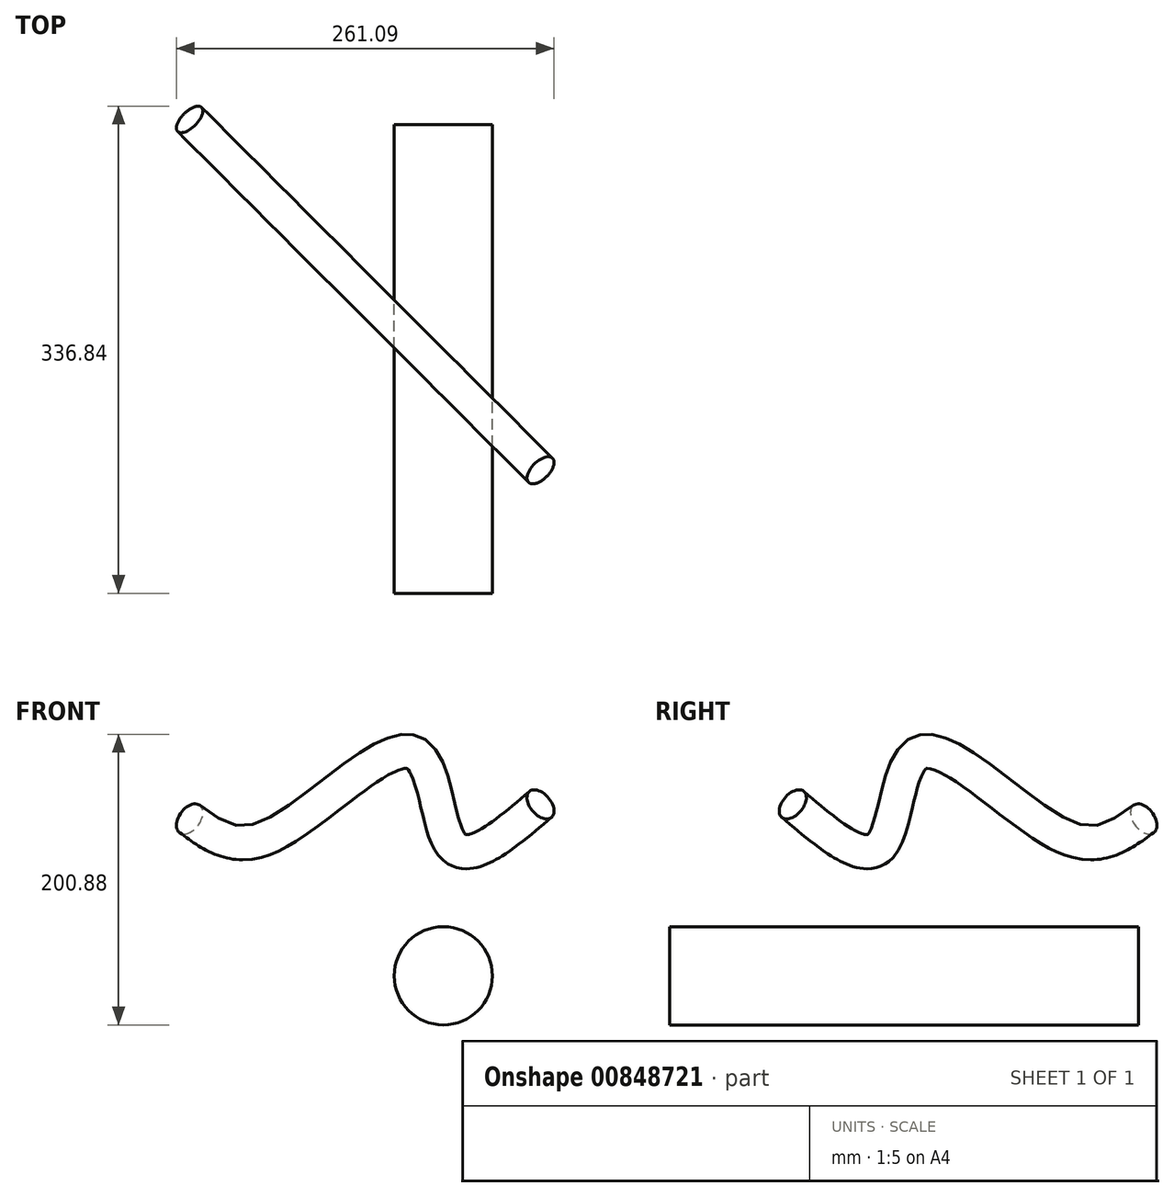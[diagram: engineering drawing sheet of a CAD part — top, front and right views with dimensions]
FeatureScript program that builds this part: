
annotation { "Feature Type Name" : "Feature", "Feature Type Description" : "" }
export const myFeature = defineFeature(function(context is Context, id is Id, definition is map)
    precondition{}
    {
        {
            var Q0;
            Q0=qCreatedBy(makeId("Front.planeOp"),FACE);
            var sketch = newSketch(context, id + "F0", { "sketchPlane" : qUnion([Q0])});
            skCircle(sketch, "E0", {"center": v(0, 0) * mm, "radius": 33.95 * mm});
            skSolve(sketch);
        }
        {
            var Q0;
            Q0 = qSketchRegion(id + "F0", true);
            extrude(context, id + "F1", {"entities" : qUnion([Q0]), "depth" : 324.1 * mm, "offsetDistance" : 25.4 * mm});
        }
        {
            var Q0;
            Q0=qCreatedBy(makeId("Right.planeOp"),FACE);
            var sketch = newSketch(context, id + "F2", { "sketchPlane" : qUnion([Q0])});
            skFitSpline(sketch, "E1", {"points": [v(76.36, 108.21) * mm, v(0, 95.44) * mm, v(-145.46, 152.9) * mm, v(-179.98, 90.26) * mm, v(-266.98, 118.27) * mm], "startDerivative": vector(-290.4, -151.51) * mm, "endDerivative": vector(-433.5, 262.42) * mm});
            skSolve(sketch);
        }
        {
            var Q0;
            Q0=sQuery(id+"F2.wireOp",EDGE,"E1");
            var Q1;
            Q1=sQuery(id+"F2.wireOp",VERTEX,"E1.2.internal");
            cPlane(context, id + "F3", {"entities" : qUnion([Q0, Q1]), "cplaneType" : CPlaneType.CURVE_POINT, "offset" : 25.4 * mm, "width" : 152.4 * mm, "height" : 152.4 * mm});
        }
        {
            var Q0;
            Q0=qCreatedBy(id+"F3.planeOp",FACE);
            var sketch = newSketch(context, id + "F4", { "sketchPlane" : qUnion([Q0])});
            skCircle(sketch, "E2", {"center": v(0, 200.08) * mm, "radius": 11.76 * mm});
            skSolve(sketch);
        }
        {
            var Q0;
            Q0=makeQuery(id+"F4.imprint","IMPRINT",FACE,{"disambiguationData":[TD([[makeQuery(id+"F4.imprint","IMPRINT",EDGE,{"derivedFrom":sQuery(id+"F4.wireOp",EDGE,"E2")}),1.0]])]});
            var Q1;
            Q1=sQuery(id+"F2.wireOp",EDGE,"E1");
            sweep(context, id + "F5", {"profiles" : qUnion([Q0]), "path" : qUnion([Q1])});
        }
        {
            var Q0;
            Q0=qCreatedBy(makeId("Top.planeOp"),FACE);
            var sketch = newSketch(context, id + "F6", { "sketchPlane" : qUnion([Q0])});
            skCircle(sketch, "E3", {"center": v(0, -171.8) * mm, "radius": 60.57 * mm});
            skSolve(sketch);
        }
        {
            var Q0;
            Q0=makeQuery(id+"F5.opSweep","SWEPT_BODY",BODY,{"disambiguationData":[OSD([sQuery(id+"F2.wireOp",EDGE,"E1"),sQuery(id+"F4.wireOp",EDGE,"E2")])]});
            var Q1;
            Q1=sQuery(id+"F6.wireOp",EDGE,"E3");
            transform(context, id + "F7", {"entities" : qUnion([Q0]), "transformType" : TransformType.ROTATION, "transformAxis" : qUnion([Q1]), "angle" : 45 * degree, "makeCopy" : false});
        }
    });
